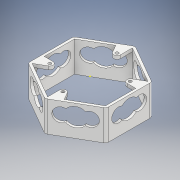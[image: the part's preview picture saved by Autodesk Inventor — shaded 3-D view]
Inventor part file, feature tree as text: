
AUTODESK INVENTOR PART (.ipt)
format: ipt  version: 2018 (Build 220112000, 112)  size: 513,024 bytes
history: native  units: mm
features: extrude x19, sketch x15, projected_geometry x14, fillet x2, hole x1, pattern_circular x1
ambient origin geometry x8: Origin, YZ Plane, XZ Plane, XY Plane, X Axis, Y Axis, Z Axis, Center Point
bodies: Solid1 (feature_tree)
feature tree (52):
  extrude  "Extrusion1"  Depth=3.0mm
  extrude  "Extrusion2"  Depth=37.0mm
  sketch  "Sketch5"  dims[d5=4.0mm d6=0.0mm d49=25.5mm]
  extrude  "Extrusion3"  Depth=4.0mm
  extrude  "Extrusion4"  Depth=11.7mm
  extrude  "Extrusion5"  Depth=23.0mm
  sketch  "Sketch9"  dims[d66=8.5mm d67=27.0mm]
  hole  "Hole3"  [1 undecoded]
  extrude  "Extrusion6"  Depth=27.0mm
  extrude  "Extrusion7"  Depth=22.0mm
  extrude  "Extrusion8"  Depth=13.0mm
  extrude  "Extrusion9"  Depth=14.5mm
  extrude  "Extrusion10"  Depth=54.864mm
  extrude  "Extrusion11"  Depth=4.5mm
  pattern_circular  "Circular Pattern1"  [2 undecoded]
  extrude  "Extrusion12"  Depth=22.0mm
  extrude  "Extrusion13"  Depth=22.0mm
  fillet  "Fillet1"  Radius=3.0mm
  fillet  "Fillet2"  Radius=3.0mm
  extrude  "Extrusion16"  Depth=3.0mm TaperAngle=0.0deg
  extrude  "Extrusion14"  Depth=3.0mm TaperAngle=0.0deg
  extrude  "Extrusion15"  Depth=3.0mm TaperAngle=0.0deg
  extrude  "Extrusion17"  Depth=3.0mm TaperAngle=0.0deg
  extrude  "Extrusion19"  Depth=4.0mm TaperAngle=360.0deg
  extrude  "Extrusion18"  Depth=10.0mm TaperAngle=0.0deg
  sketch  "Sketch1"  dims[d0=54.864mm d1=3.0mm]
  sketch  "Sketch2"  dims[d2=37.0mm d3=0.0mm d4=15.25mm]
  sketch  "Sketch6"  dims[d51=8.44mm d53=11.7mm]
  projected_geometry  "Projected Loop1"
  sketch  "Sketch7"  dims[d54=15.0mm d55=23.0mm]
  projected_geometry  "Projected Loop2"
  sketch  "Sketch8"  dims[d56=3.0mm d57=0.0mm d58=14.5mm]
  projected_geometry  "Projected Loop3"
  projected_geometry  "Projected Loop4"
  projected_geometry  "Projected Loop5"
  projected_geometry  "Projected Loop6"
  projected_geometry  "Projected Loop7"
  sketch  "Sketch10"  dims[d68=14.5mm d70=22.0mm]
  projected_geometry  "Projected Loop8"
  projected_geometry  "Projected Loop9"
  projected_geometry  "Projected Loop10"
  projected_geometry  "Projected Loop11"
  projected_geometry  "Projected Loop12"
  projected_geometry  "Projected Loop13"
  sketch  "Sketch11"  dims[d71=15.0mm d72=13.0mm]
  projected_geometry  "Projected Loop14"
  sketch  "Sketch12"  dims[d73=3.0mm d74=0.0mm]
  sketch  "Sketch13"  dims[d75=27.0mm d76=8.5mm d77=11.0mm d78=13.0mm d79=15.0mm d81=14.5mm]
  sketch  "Sketch14"  dims[d82=54.864mm d83=54.864mm]
  sketch  "Sketch15"  dims[d84=3.0mm d85=0.0mm]
  sketch  "Sketch16"  dims[d86=3.1mm d87=39.0mm d88=4.5mm d89=4.5mm d90=4.5mm d91=4.5mm d92=4.5mm d93=4.5mm d94=4.5mm d95=4.5mm d96=4.5mm d97=4.5mm d98=4.5mm]
  sketch  "Sketch17"  dims[d99=4.5mm d100=22.0mm d101=22.0mm d102=22.0mm d103=3.7mm d104=6.0mm d105=4.0mm d106=2.0mm d107=90.0deg d108=8.0mm d109=20.594885mm d110=3.0mm d111=0.0mm d112=3.0mm d113=0.0mm d114=3.0mm d115=0.0mm d116=3.0mm d117=0.0mm d118=3.0mm d119=0.0mm d120=3.0mm d121=0.0mm d122=60.0mm d123=360.0deg d125=10.0mm d126=0.0mm d127=10.0mm d128=0.0mm d129=4.0mm d130=4.0mm d131=0.4mm d132=0.0mm d133=0.4mm d134=0.0mm d135=0.4mm d136=0.0mm d137=0.4mm d138=0.0mm d139=0.4mm d140=0.0mm d141=0.4mm d142=0.0mm d29=1.0mm d30=1.0mm d143=1.0mm d144=1.0mm]
note: 3 required parameter values undecoded (feature->parameter linkage not recoverable at this tier; creation-order binding heuristic only, values carry confidence <= 0.55)
